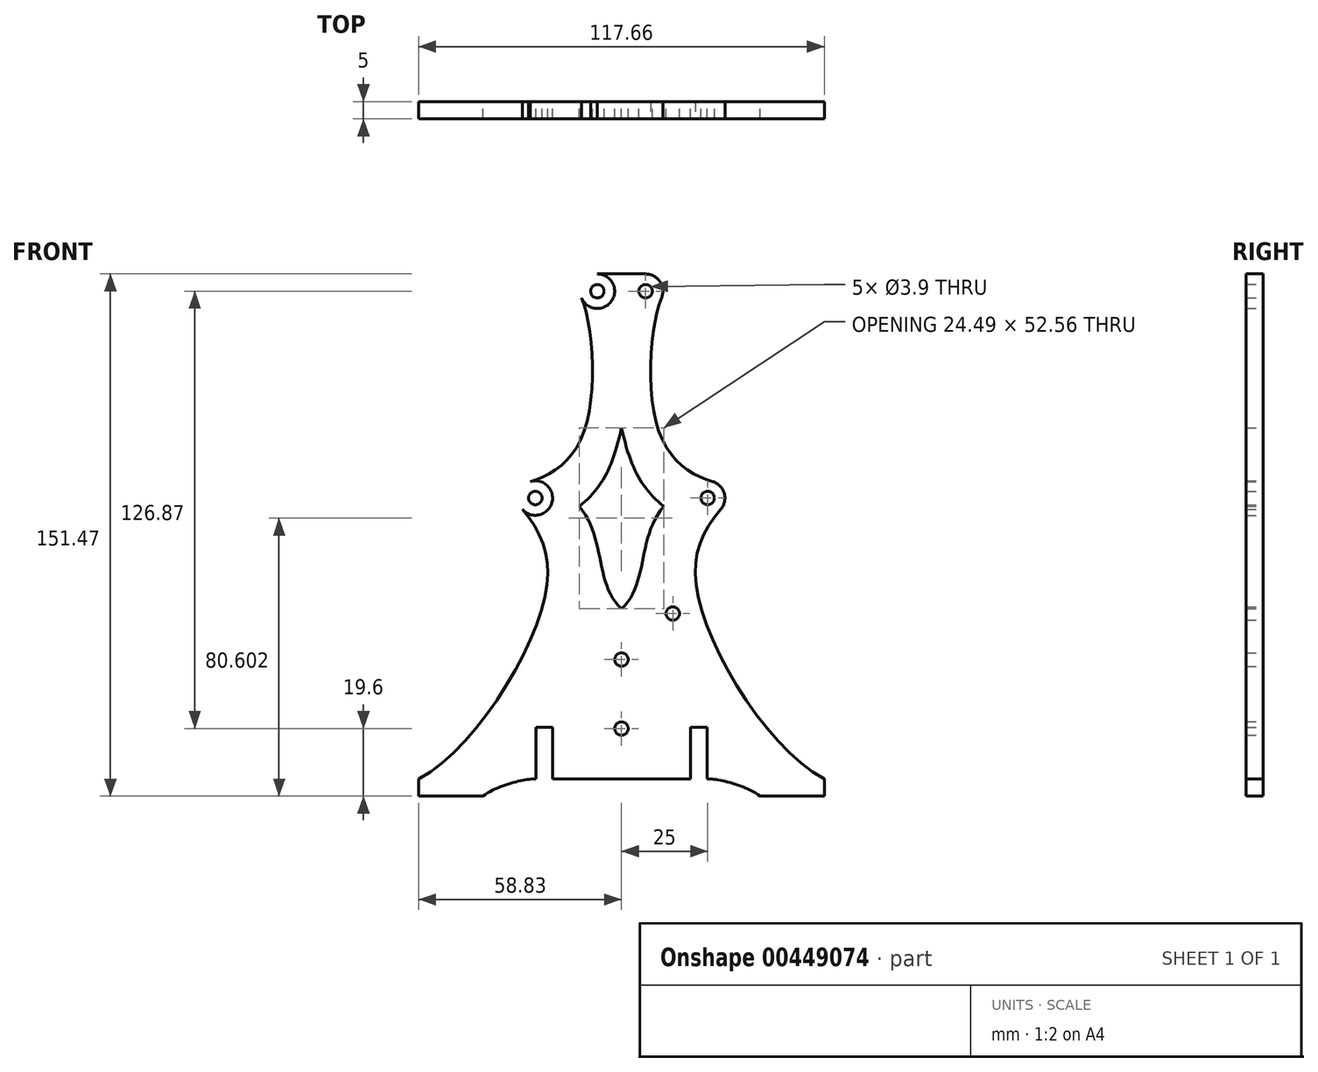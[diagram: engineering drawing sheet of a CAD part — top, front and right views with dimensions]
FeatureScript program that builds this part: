
annotation { "Feature Type Name" : "Feature", "Feature Type Description" : "" }
export const myFeature = defineFeature(function(context is Context, id is Id, definition is map)
    precondition{}
    {
        {
            var Q0;
            Q0=qCreatedBy(makeId("Front.planeOp"),FACE);
            var sketch = newSketch(context, id + "F0", { "sketchPlane" : qUnion([Q0])});
            skPoint(sketch, "E0", {"position": v(7, 60) * mm});
            skPoint(sketch, "E1", {"position": v(25, 0) * mm});
            skCircle(sketch, "E2", {"center": v(7, 60) * mm, "radius": 1.95 * mm});
            skCircle(sketch, "E3", {"center": v(7, 60) * mm, "radius": 5 * mm});
            skCircle(sketch, "E4", {"center": v(25, 0) * mm, "radius": 1.95 * mm});
            skCircle(sketch, "E5", {"center": v(25, 0) * mm, "radius": 5 * mm});
            skLineSegment(sketch, "E6", {"start": v(7, 65) * mm, "end": v(0, 65) * mm});
            skFitSpline(sketch, "E7", {"points": [v(11.6, 58.03) * mm, v(11.18, 18.46) * mm, v(26.44, 4.79) * mm], "startDerivative": vector(-17.22, -40.25) * mm, "endDerivative": vector(42.1, -12.66) * mm});
            skLineSegment(sketch, "E8", {"start": v(0, -86.47) * mm, "end": v(58.83, -86.47) * mm});
            skLineSegment(sketch, "E9", {"start": v(58.83, -86.47) * mm, "end": v(58.83, -81.47) * mm});
            skFitSpline(sketch, "E10", {"points": [v(28.8, -3.24) * mm, v(22.3, -28.9) * mm, v(58.83, -81.47) * mm], "startDerivative": vector(-46.6, -54.68) * mm, "endDerivative": vector(76.87, -40.6) * mm});
            skCircle(sketch, "E11.MirrorC", {"center": v(-25, 0) * mm, "radius": 5 * mm});
            skCircle(sketch, "E12.MirrorC", {"center": v(-7, 60) * mm, "radius": 1.95 * mm});
            skCircle(sketch, "E13.MirrorC", {"center": v(-25, 0) * mm, "radius": 1.95 * mm});
            skLineSegment(sketch, "E14.MirrorCS", {"start": v(-58.83, -86.47) * mm, "end": v(-58.83, -81.47) * mm});
            skLineSegment(sketch, "E15.MirrorCS", {"start": v(0, -86.47) * mm, "end": v(-58.83, -86.47) * mm});
            skLineSegment(sketch, "E16.MirrorCS", {"start": v(-7, 65) * mm, "end": v(0, 65) * mm});
            skCircle(sketch, "E17.MirrorC", {"center": v(-7, 60) * mm, "radius": 5 * mm});
            skFitSpline(sketch, "E18.MirrorCS", {"points": [v(-28.8, -3.24) * mm, v(-22.3, -28.9) * mm, v(-58.83, -81.47) * mm], "startDerivative": vector(46.6, -54.68) * mm, "endDerivative": vector(-76.87, -40.6) * mm});
            skFitSpline(sketch, "E19.MirrorCS", {"points": [v(-11.6, 58.03) * mm, v(-11.18, 18.46) * mm, v(-26.44, 4.79) * mm], "startDerivative": vector(17.22, -40.25) * mm, "endDerivative": vector(-42.1, -12.66) * mm});
            skPoint(sketch, "E20", {"position": v(0, -46.87) * mm});
            skPoint(sketch, "E21", {"position": v(14.88, -33.5) * mm});
            skCircle(sketch, "E22", {"center": v(14.88, -33.5) * mm, "radius": 1.95 * mm});
            skCircle(sketch, "E23", {"center": v(0, -46.87) * mm, "radius": 1.95 * mm});
            skPoint(sketch, "E24", {"position": v(0, -66.87) * mm});
            skCircle(sketch, "E25", {"center": v(0, -66.87) * mm, "radius": 1.95 * mm});
            skLineSegment(sketch, "E26.bottom", {"start": v(20, -86.47) * mm, "end": v(24.8, -86.47) * mm});
            skLineSegment(sketch, "E26.top", {"start": v(20, -66.47) * mm, "end": v(24.8, -66.47) * mm});
            skLineSegment(sketch, "E26.left", {"start": v(20, -86.47) * mm, "end": v(20, -66.47) * mm});
            skLineSegment(sketch, "E26.right", {"start": v(24.8, -86.47) * mm, "end": v(24.8, -66.47) * mm});
            skLineSegment(sketch, "E27.MirrorCS", {"start": v(-20, -86.47) * mm, "end": v(-24.8, -86.47) * mm});
            skLineSegment(sketch, "E28.MirrorCS", {"start": v(-24.8, -86.47) * mm, "end": v(-24.8, -66.47) * mm});
            skLineSegment(sketch, "E29.MirrorCS", {"start": v(-20, -86.47) * mm, "end": v(-20, -66.47) * mm});
            skLineSegment(sketch, "E30.MirrorCS", {"start": v(-20, -66.47) * mm, "end": v(-24.8, -66.47) * mm});
            skFitSpline(sketch, "E31", {"points": [v(0, 20.41) * mm, v(12.25, -2.43) * mm], "startDerivative": vector(7.79, -35.3) * mm, "endDerivative": vector(19.68, -16.26) * mm});
            skFitSpline(sketch, "E32", {"points": [v(12.25, -2.43) * mm, v(0, -32.15) * mm], "startDerivative": vector(-23.52, -27.62) * mm, "endDerivative": vector(-23.87, -22.09) * mm});
            skFitSpline(sketch, "E33.MirrorCS", {"points": [v(0, 20.41) * mm, v(-12.25, -2.43) * mm], "startDerivative": vector(-7.79, -35.3) * mm, "endDerivative": vector(-19.68, -16.26) * mm});
            skFitSpline(sketch, "E34.MirrorCS", {"points": [v(-12.25, -2.43) * mm, v(0, -32.15) * mm], "startDerivative": vector(23.52, -27.62) * mm, "endDerivative": vector(23.87, -22.09) * mm});
            skFitSpline(sketch, "E35", {"points": [v(24.8, -81.47) * mm, v(40.23, -86.47) * mm], "startDerivative": vector(9.1, 0.12) * mm, "endDerivative": vector(14.85, -10.38) * mm});
            skLineSegment(sketch, "E36", {"start": v(20, -81.47) * mm, "end": v(0, -81.47) * mm});
            skLineSegment(sketch, "E37.MirrorCS", {"start": v(-20, -81.47) * mm, "end": v(0, -81.47) * mm});
            skFitSpline(sketch, "E38.MirrorCS", {"points": [v(-24.8, -81.47) * mm, v(-40.23, -86.47) * mm], "startDerivative": vector(-9.1, 0.12) * mm, "endDerivative": vector(-14.85, -10.38) * mm});
            skSolve(sketch);
        }
        {
            var Q0;
            {var subQ4=sQuery(id+"F0.wireOp",EDGE,"E6");Q0=makeQuery(id+"F0.imprint","IMPRINT",FACE,{"disambiguationData":[TD([[makeQuery(id+"F0.imprint","IMPRINT",EDGE,{"derivedFrom":subQ4}),1.0]])]});}
            var Q1;
            Q1=makeQuery(id+"F0.imprint","IMPRINT",FACE,{"disambiguationData":[TD([[makeQuery(id+"F0.imprint","IMPRINT",EDGE,{"derivedFrom":sQuery(id+"F0.wireOp",EDGE,"E2")}),-1.0]])]});
            var Q2;
            Q2=makeQuery(id+"F0.imprint","IMPRINT",FACE,{"disambiguationData":[TD([[makeQuery(id+"F0.imprint","IMPRINT",EDGE,{"derivedFrom":sQuery(id+"F0.wireOp",EDGE,"E4")}),-1.0]])]});
            var Q3;
            Q3=makeQuery(id+"F0.imprint","IMPRINT",FACE,{"disambiguationData":[TD([[makeQuery(id+"F0.imprint","IMPRINT",EDGE,{"derivedFrom":sQuery(id+"F0.wireOp",EDGE,"E12.MirrorC")}),1.0]])]});
            var Q4;
            Q4=makeQuery(id+"F0.imprint","IMPRINT",FACE,{"disambiguationData":[TD([[makeQuery(id+"F0.imprint","IMPRINT",EDGE,{"derivedFrom":sQuery(id+"F0.wireOp",EDGE,"E13.MirrorC")}),1.0]])]});
            var Q5;
            {var subQ4=sQuery(id+"F0.wireOp",EDGE,"E7");Q5=makeQuery(id+"F0.imprint","IMPRINT",FACE,{"disambiguationData":[TD([[makeQuery(id+"F0.imprint","IMPRINT",EDGE,{"derivedFrom":subQ4}),-1.0]])]});}
            extrude(context, id + "F1", {"entities" : qUnion([Q0, Q1, Q2, Q3, Q4, Q5]), "depth" : 5 * mm});
        }
    });
